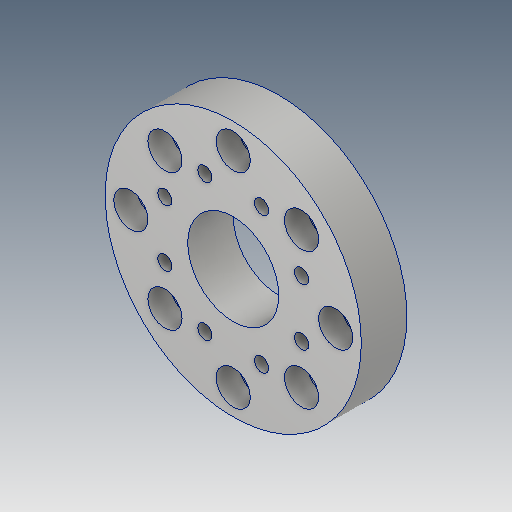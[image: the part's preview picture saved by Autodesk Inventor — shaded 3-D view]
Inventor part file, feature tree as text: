
AUTODESK INVENTOR PART (.ipt)
format: ipt  version: 2020.5 (Build 245400000, 400)  size: 225,280 bytes
history: native  units: mm
features: extrude x5, sketch x5, other x1, projected_geometry x1
ambient origin geometry x8: Origin, YZ Plane, XZ Plane, XY Plane, X Axis, Y Axis, Z Axis, Center Point
bodies: Body1 (feature_tree)
feature tree (12):
  other  "솔리드1"
  extrude  "돌출1"  Depth=45.0mm
  extrude  "돌출2"  Depth=8.0mm TaperAngle=0.0deg
  extrude  "돌출3"  Depth=16.0mm
  extrude  "돌출4"  Depth=16.0mm
  extrude  "돌출5"  TaperAngle=0.0deg  [1 undecoded]
  sketch  "스케치1"
  sketch  "스케치2"
  sketch  "스케치3"
  sketch  "스케치4"
  projected_geometry  "투영된 루프1"
  sketch  "스케치5"
note: 1 required parameter value undecoded (feature->parameter linkage not recoverable at this tier; creation-order binding heuristic only, values carry confidence <= 0.55)
